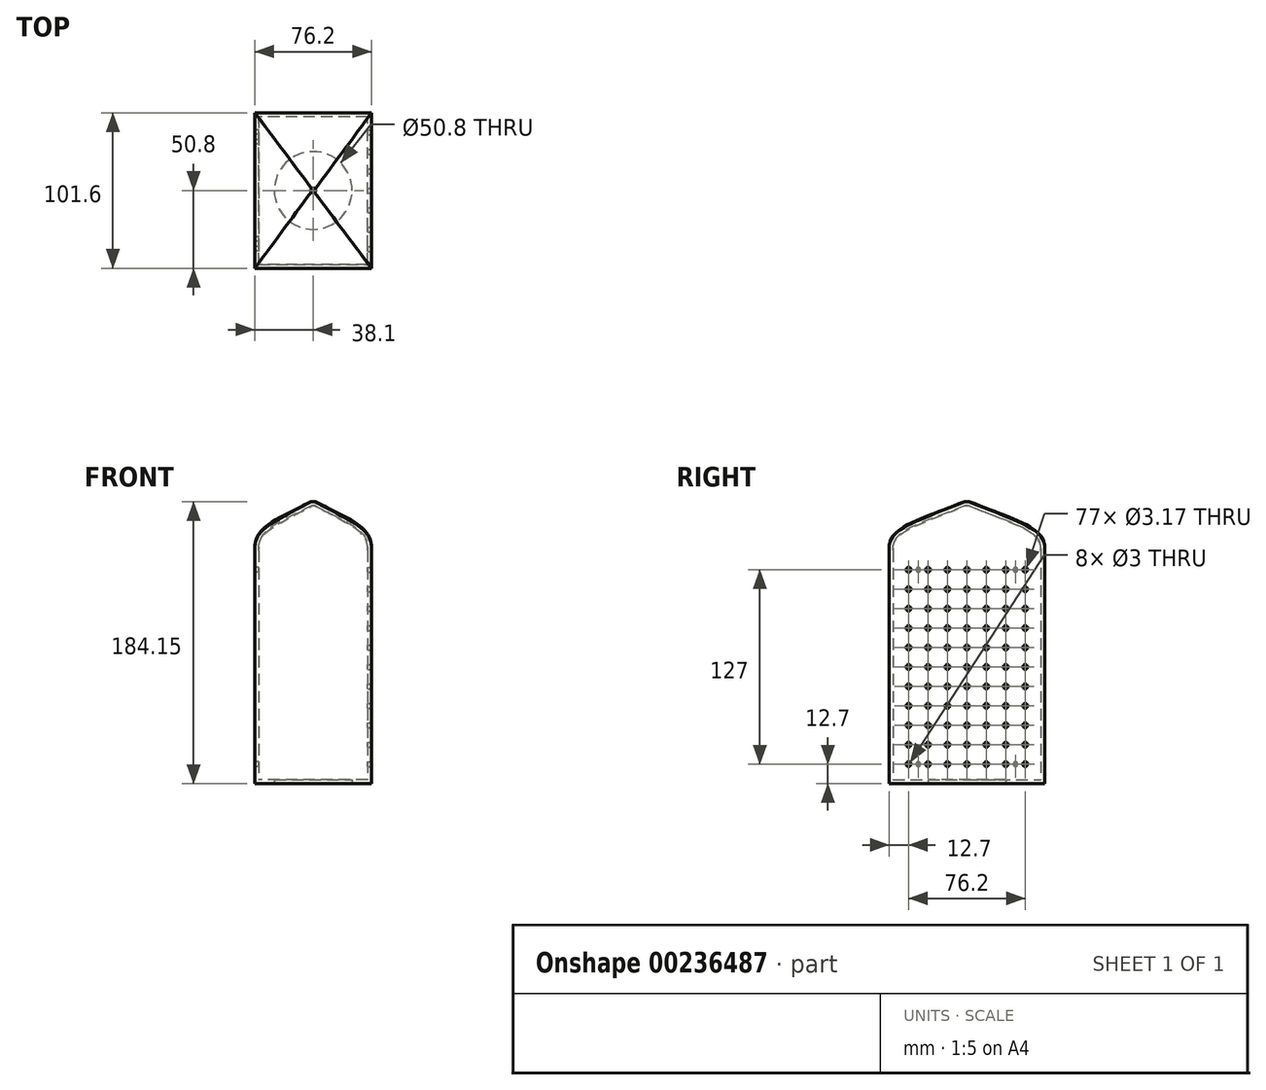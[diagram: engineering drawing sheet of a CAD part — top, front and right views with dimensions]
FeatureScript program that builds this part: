
annotation { "Feature Type Name" : "Feature", "Feature Type Description" : "" }
export const myFeature = defineFeature(function(context is Context, id is Id, definition is map)
    precondition{}
    {
        {
            var Q0;
            Q0=qCreatedBy(makeId("Top.planeOp"),FACE);
            var sketch = newSketch(context, id + "F0", { "sketchPlane" : qUnion([Q0])});
            skLineSegment(sketch, "E0.bottom", {"start": v(-38.1, 50.8) * mm, "end": v(38.1, 50.8) * mm});
            skLineSegment(sketch, "E0.top", {"start": v(-38.1, -50.8) * mm, "end": v(38.1, -50.8) * mm});
            skLineSegment(sketch, "E0.left", {"start": v(-38.1, 50.8) * mm, "end": v(-38.1, -50.8) * mm});
            skLineSegment(sketch, "E0.right", {"start": v(38.1, 50.8) * mm, "end": v(38.1, -50.8) * mm});
            skLineSegment(sketch, "E1", {"start": v(-38.1, 50.8) * mm, "end": v(38.1, -50.8) * mm, "construction": true});
            skSolve(sketch);
        }
        {
            var Q0;
            Q0=qSketchRegion(id+"F0",true);
            extrude(context, id + "F1", {"entities" : qUnion([Q0]), "depth" : 152.4 * mm});
        }
        {
            var Q0;
            Q0=makeQuery(id+"F1.opExtrude","SWEPT_FACE",FACE,{"disambiguationData":[OSD([sQuery(id+"F0.wireOp",EDGE,"E0.right")])]});
            var sketch = newSketch(context, id + "F2", { "sketchPlane" : qUnion([Q0])});
            skCircle(sketch, "E2", {"center": v(-38.1, 139.7) * mm, "radius": 1.59 * mm});
            skCircle(sketch, "E3.1.0.0", {"center": v(-38.1, 127) * mm, "radius": 1.59 * mm});
            skCircle(sketch, "E3.2.0.0", {"center": v(-38.1, 114.3) * mm, "radius": 1.59 * mm});
            skLineSegment(sketch, "E3.direction1", {"start": v(-38.1, 139.7) * mm, "end": v(-38.1, 127) * mm, "construction": true});
            skCircle(sketch, "E4.0.3.0", {"center": v(-38.1, 101.6) * mm, "radius": 1.59 * mm});
            skCircle(sketch, "E4.0.4.0", {"center": v(-38.1, 88.9) * mm, "radius": 1.59 * mm});
            skCircle(sketch, "E4.0.5.0", {"center": v(-38.1, 76.2) * mm, "radius": 1.59 * mm});
            skCircle(sketch, "E4.0.6.0", {"center": v(-38.1, 63.5) * mm, "radius": 1.59 * mm});
            skCircle(sketch, "E4.0.7.0", {"center": v(-38.1, 50.8) * mm, "radius": 1.59 * mm});
            skCircle(sketch, "E4.0.8.0", {"center": v(-38.1, 38.1) * mm, "radius": 1.59 * mm});
            skCircle(sketch, "E4.0.9.0", {"center": v(-38.1, 25.4) * mm, "radius": 1.59 * mm});
            skCircle(sketch, "E5.0.10.0", {"center": v(-38.1, 12.7) * mm, "radius": 1.59 * mm});
            skCircle(sketch, "E6.1.0.0", {"center": v(-25.4, 139.7) * mm, "radius": 1.59 * mm});
            skCircle(sketch, "E6.1.0.1", {"center": v(-25.4, 127) * mm, "radius": 1.59 * mm});
            skCircle(sketch, "E6.1.0.2", {"center": v(-25.4, 114.3) * mm, "radius": 1.59 * mm});
            skCircle(sketch, "E6.1.0.3", {"center": v(-25.4, 101.6) * mm, "radius": 1.59 * mm});
            skCircle(sketch, "E6.1.0.4", {"center": v(-25.4, 88.9) * mm, "radius": 1.59 * mm});
            skCircle(sketch, "E6.1.0.5", {"center": v(-25.4, 63.5) * mm, "radius": 1.59 * mm});
            skCircle(sketch, "E6.1.0.6", {"center": v(-25.4, 12.7) * mm, "radius": 1.59 * mm});
            skCircle(sketch, "E6.1.0.7", {"center": v(-25.4, 25.4) * mm, "radius": 1.59 * mm});
            skCircle(sketch, "E6.1.0.8", {"center": v(-25.4, 76.2) * mm, "radius": 1.59 * mm});
            skCircle(sketch, "E6.1.0.9", {"center": v(-25.4, 38.1) * mm, "radius": 1.59 * mm});
            skCircle(sketch, "E6.1.0.10", {"center": v(-25.4, 50.8) * mm, "radius": 1.59 * mm});
            skCircle(sketch, "E6.2.0.0", {"center": v(-12.7, 139.7) * mm, "radius": 1.59 * mm});
            skCircle(sketch, "E6.2.0.1", {"center": v(-12.7, 127) * mm, "radius": 1.59 * mm});
            skCircle(sketch, "E6.2.0.2", {"center": v(-12.7, 114.3) * mm, "radius": 1.59 * mm});
            skCircle(sketch, "E6.2.0.3", {"center": v(-12.7, 101.6) * mm, "radius": 1.59 * mm});
            skCircle(sketch, "E6.2.0.4", {"center": v(-12.7, 88.9) * mm, "radius": 1.59 * mm});
            skCircle(sketch, "E6.2.0.5", {"center": v(-12.7, 63.5) * mm, "radius": 1.59 * mm});
            skCircle(sketch, "E6.2.0.6", {"center": v(-12.7, 12.7) * mm, "radius": 1.59 * mm});
            skCircle(sketch, "E6.2.0.7", {"center": v(-12.7, 25.4) * mm, "radius": 1.59 * mm});
            skCircle(sketch, "E6.2.0.8", {"center": v(-12.7, 76.2) * mm, "radius": 1.59 * mm});
            skCircle(sketch, "E6.2.0.9", {"center": v(-12.7, 38.1) * mm, "radius": 1.59 * mm});
            skCircle(sketch, "E6.2.0.10", {"center": v(-12.7, 50.8) * mm, "radius": 1.59 * mm});
            skCircle(sketch, "E6.3.0.0", {"center": v(0, 139.7) * mm, "radius": 1.59 * mm});
            skCircle(sketch, "E6.3.0.1", {"center": v(0, 127) * mm, "radius": 1.59 * mm});
            skCircle(sketch, "E6.3.0.2", {"center": v(0, 114.3) * mm, "radius": 1.59 * mm});
            skCircle(sketch, "E6.3.0.3", {"center": v(0, 101.6) * mm, "radius": 1.59 * mm});
            skCircle(sketch, "E6.3.0.4", {"center": v(0, 88.9) * mm, "radius": 1.59 * mm});
            skCircle(sketch, "E6.3.0.5", {"center": v(0, 63.5) * mm, "radius": 1.59 * mm});
            skCircle(sketch, "E6.3.0.6", {"center": v(0, 12.7) * mm, "radius": 1.59 * mm});
            skCircle(sketch, "E6.3.0.7", {"center": v(0, 25.4) * mm, "radius": 1.59 * mm});
            skCircle(sketch, "E6.3.0.8", {"center": v(0, 76.2) * mm, "radius": 1.59 * mm});
            skCircle(sketch, "E6.3.0.9", {"center": v(0, 38.1) * mm, "radius": 1.59 * mm});
            skCircle(sketch, "E6.3.0.10", {"center": v(0, 50.8) * mm, "radius": 1.59 * mm});
            skCircle(sketch, "E6.4.0.0", {"center": v(12.7, 139.7) * mm, "radius": 1.59 * mm});
            skCircle(sketch, "E6.4.0.1", {"center": v(12.7, 127) * mm, "radius": 1.59 * mm});
            skCircle(sketch, "E6.4.0.2", {"center": v(12.7, 114.3) * mm, "radius": 1.59 * mm});
            skCircle(sketch, "E6.4.0.3", {"center": v(12.7, 101.6) * mm, "radius": 1.59 * mm});
            skCircle(sketch, "E6.4.0.4", {"center": v(12.7, 88.9) * mm, "radius": 1.59 * mm});
            skCircle(sketch, "E6.4.0.5", {"center": v(12.7, 63.5) * mm, "radius": 1.59 * mm});
            skCircle(sketch, "E6.4.0.6", {"center": v(12.7, 12.7) * mm, "radius": 1.59 * mm});
            skCircle(sketch, "E6.4.0.7", {"center": v(12.7, 25.4) * mm, "radius": 1.59 * mm});
            skCircle(sketch, "E6.4.0.8", {"center": v(12.7, 76.2) * mm, "radius": 1.59 * mm});
            skCircle(sketch, "E6.4.0.9", {"center": v(12.7, 38.1) * mm, "radius": 1.59 * mm});
            skCircle(sketch, "E6.4.0.10", {"center": v(12.7, 50.8) * mm, "radius": 1.59 * mm});
            skCircle(sketch, "E6.5.0.0", {"center": v(25.4, 139.7) * mm, "radius": 1.59 * mm});
            skCircle(sketch, "E6.5.0.1", {"center": v(25.4, 127) * mm, "radius": 1.59 * mm});
            skCircle(sketch, "E6.5.0.2", {"center": v(25.4, 114.3) * mm, "radius": 1.59 * mm});
            skCircle(sketch, "E6.5.0.3", {"center": v(25.4, 101.6) * mm, "radius": 1.59 * mm});
            skCircle(sketch, "E6.5.0.4", {"center": v(25.4, 88.9) * mm, "radius": 1.59 * mm});
            skCircle(sketch, "E6.5.0.5", {"center": v(25.4, 63.5) * mm, "radius": 1.59 * mm});
            skCircle(sketch, "E6.5.0.6", {"center": v(25.4, 12.7) * mm, "radius": 1.59 * mm});
            skCircle(sketch, "E6.5.0.7", {"center": v(25.4, 25.4) * mm, "radius": 1.59 * mm});
            skCircle(sketch, "E6.5.0.8", {"center": v(25.4, 76.2) * mm, "radius": 1.59 * mm});
            skCircle(sketch, "E6.5.0.9", {"center": v(25.4, 38.1) * mm, "radius": 1.59 * mm});
            skCircle(sketch, "E6.5.0.10", {"center": v(25.4, 50.8) * mm, "radius": 1.59 * mm});
            skCircle(sketch, "E6.6.0.0", {"center": v(38.1, 139.7) * mm, "radius": 1.59 * mm});
            skCircle(sketch, "E6.6.0.1", {"center": v(38.1, 127) * mm, "radius": 1.59 * mm});
            skCircle(sketch, "E6.6.0.2", {"center": v(38.1, 114.3) * mm, "radius": 1.59 * mm});
            skCircle(sketch, "E6.6.0.3", {"center": v(38.1, 101.6) * mm, "radius": 1.59 * mm});
            skCircle(sketch, "E6.6.0.4", {"center": v(38.1, 88.9) * mm, "radius": 1.59 * mm});
            skCircle(sketch, "E6.6.0.5", {"center": v(38.1, 63.5) * mm, "radius": 1.59 * mm});
            skCircle(sketch, "E6.6.0.6", {"center": v(38.1, 12.7) * mm, "radius": 1.59 * mm});
            skCircle(sketch, "E6.6.0.7", {"center": v(38.1, 25.4) * mm, "radius": 1.59 * mm});
            skCircle(sketch, "E6.6.0.8", {"center": v(38.1, 76.2) * mm, "radius": 1.59 * mm});
            skCircle(sketch, "E6.6.0.9", {"center": v(38.1, 38.1) * mm, "radius": 1.59 * mm});
            skCircle(sketch, "E6.6.0.10", {"center": v(38.1, 50.8) * mm, "radius": 1.59 * mm});
            skLineSegment(sketch, "E6.direction1", {"start": v(-38.1, 139.7) * mm, "end": v(-25.4, 139.7) * mm, "construction": true});
            skSolve(sketch);
        }
        {
            var Q0;
            Q0=makeQuery(id+"F1.opExtrude","CAP_FACE",FACE,{"disambiguationData":[OSD([sQuery(id+"F0.wireOp",EDGE,"E0.bottom"),sQuery(id+"F0.wireOp",EDGE,"E0.top"),sQuery(id+"F0.wireOp",EDGE,"E0.left"),sQuery(id+"F0.wireOp",EDGE,"E0.right")])],"isStart":false});
            cPlane(context, id + "F3", {"entities" : qUnion([Q0]), "cplaneType" : CPlaneType.OFFSET, "offset" : 31.75 * mm, "width" : 152.4 * mm, "height" : 152.4 * mm});
        }
        {
            var Q0;
            Q0=qCreatedBy(id+"F3.planeOp",FACE);
            var sketch = newSketch(context, id + "F4", { "sketchPlane" : qUnion([Q0])});
            skCircle(sketch, "E7", {"center": v(0, 0) * mm, "radius": 1.59 * mm});
            skSolve(sketch);
        }
        {
            var Q1;
            Q1=makeQuery(id+"F1.opExtrude","CAP_FACE",FACE,{"disambiguationData":[OSD([sQuery(id+"F0.wireOp",EDGE,"E0.bottom"),sQuery(id+"F0.wireOp",EDGE,"E0.top"),sQuery(id+"F0.wireOp",EDGE,"E0.left"),sQuery(id+"F0.wireOp",EDGE,"E0.right")])],"isStart":false});
            var Q2;
            Q2=makeQuery(id+"F4.imprint","IMPRINT",FACE,{"disambiguationData":[TD([[makeQuery(id+"F4.imprint","IMPRINT",EDGE,{"derivedFrom":sQuery(id+"F4.wireOp",EDGE,"E7")}),1.0]])]});
            loft(context, id + "F5", {"operationType" : NewBodyOperationType.ADD, "startCondition" : LoftEndDerivativeType.MATCH_CURVATURE, "startMagnitude" : 1, "sheetProfilesArray" : [{ "sheetProfileEntities" : qUnion([Q1]) }, { "sheetProfileEntities" : qUnion([Q2]) }]});
        }
        {
            var Q0;
            Q0=makeQuery(id+"F1.opExtrude","CAP_FACE",FACE,{"disambiguationData":[OSD([sQuery(id+"F0.wireOp",EDGE,"E0.bottom"),sQuery(id+"F0.wireOp",EDGE,"E0.top"),sQuery(id+"F0.wireOp",EDGE,"E0.left"),sQuery(id+"F0.wireOp",EDGE,"E0.right")])],"isStart":true});
            shell(context, id + "F6", {"entities" : qUnion([Q0]), "thickness" : 2.54 * mm});
        }
        {
            var Q0;
            Q0=qSketchRegion(id+"F2",true);
            extrude(context, id + "F7", {"entities" : qUnion([Q0]), "operationType" : NewBodyOperationType.REMOVE, "oppositeDirection" : true, "depth" : 25.4 * mm});
        }
        {
            var Q0;
            Q0=makeQuery(id+"F1.opExtrude","CAP_FACE",FACE,{"disambiguationData":[OSD([sQuery(id+"F0.wireOp",EDGE,"E0.bottom"),sQuery(id+"F0.wireOp",EDGE,"E0.top"),sQuery(id+"F0.wireOp",EDGE,"E0.left"),sQuery(id+"F0.wireOp",EDGE,"E0.right")])],"isStart":true});
            var sketch = newSketch(context, id + "F8", { "sketchPlane" : qUnion([Q0])});
            skLineSegment(sketch, "E8.bottom", {"start": v(38.1, 50.8) * mm, "end": v(-38.1, 50.8) * mm});
            skLineSegment(sketch, "E8.top", {"start": v(38.1, -50.8) * mm, "end": v(-38.1, -50.8) * mm});
            skLineSegment(sketch, "E8.left", {"start": v(38.1, 50.8) * mm, "end": v(38.1, -50.8) * mm});
            skLineSegment(sketch, "E8.right", {"start": v(-38.1, 50.8) * mm, "end": v(-38.1, -50.8) * mm});
            skCircle(sketch, "E9", {"center": v(0, 0) * mm, "radius": 25.4 * mm});
            skSolve(sketch);
        }
        {
            var Q0;
            Q0=qSketchRegion(id+"F8",true);
            extrude(context, id + "F9", {"entities" : qUnion([Q0]), "operationType" : NewBodyOperationType.ADD, "oppositeDirection" : true, "depth" : 2.54 * mm});
        }
        {
            var Q0;
            Q0=makeQuery(id+"F1.opExtrude","SWEPT_FACE",FACE,{"disambiguationData":[OSD([sQuery(id+"F0.wireOp",EDGE,"E0.left")])]});
            var sketch = newSketch(context, id + "F10", { "sketchPlane" : qUnion([Q0])});
            skCircle(sketch, "E10", {"center": v(-38.1, 139.7) * mm, "radius": 1.5 * mm});
            skCircle(sketch, "E11", {"center": v(-31.75, 139.7) * mm, "radius": 1.5 * mm});
            skLineSegment(sketch, "E12", {"start": v(0, 152.4) * mm, "end": v(0, 0) * mm, "construction": true});
            skLineSegment(sketch, "E13", {"start": v(-50.8, 76.2) * mm, "end": v(50.8, 76.2) * mm, "construction": true});
            skCircle(sketch, "E14.MirrorC", {"center": v(38.1, 139.7) * mm, "radius": 1.5 * mm});
            skCircle(sketch, "E15.MirrorC", {"center": v(31.75, 139.7) * mm, "radius": 1.5 * mm});
            skCircle(sketch, "E16.MirrorC", {"center": v(-38.1, 12.7) * mm, "radius": 1.5 * mm});
            skCircle(sketch, "E17.MirrorC", {"center": v(-31.75, 12.7) * mm, "radius": 1.5 * mm});
            skCircle(sketch, "E18.MirrorC", {"center": v(38.1, 12.7) * mm, "radius": 1.5 * mm});
            skCircle(sketch, "E19.MirrorC", {"center": v(31.75, 12.7) * mm, "radius": 1.5 * mm});
            skSolve(sketch);
        }
        {
            var Q0;
            Q0=qSketchRegion(id+"F10",true);
            extrude(context, id + "F11", {"entities" : qUnion([Q0]), "operationType" : NewBodyOperationType.REMOVE, "oppositeDirection" : true, "depth" : 25.4 * mm});
        }
    });
